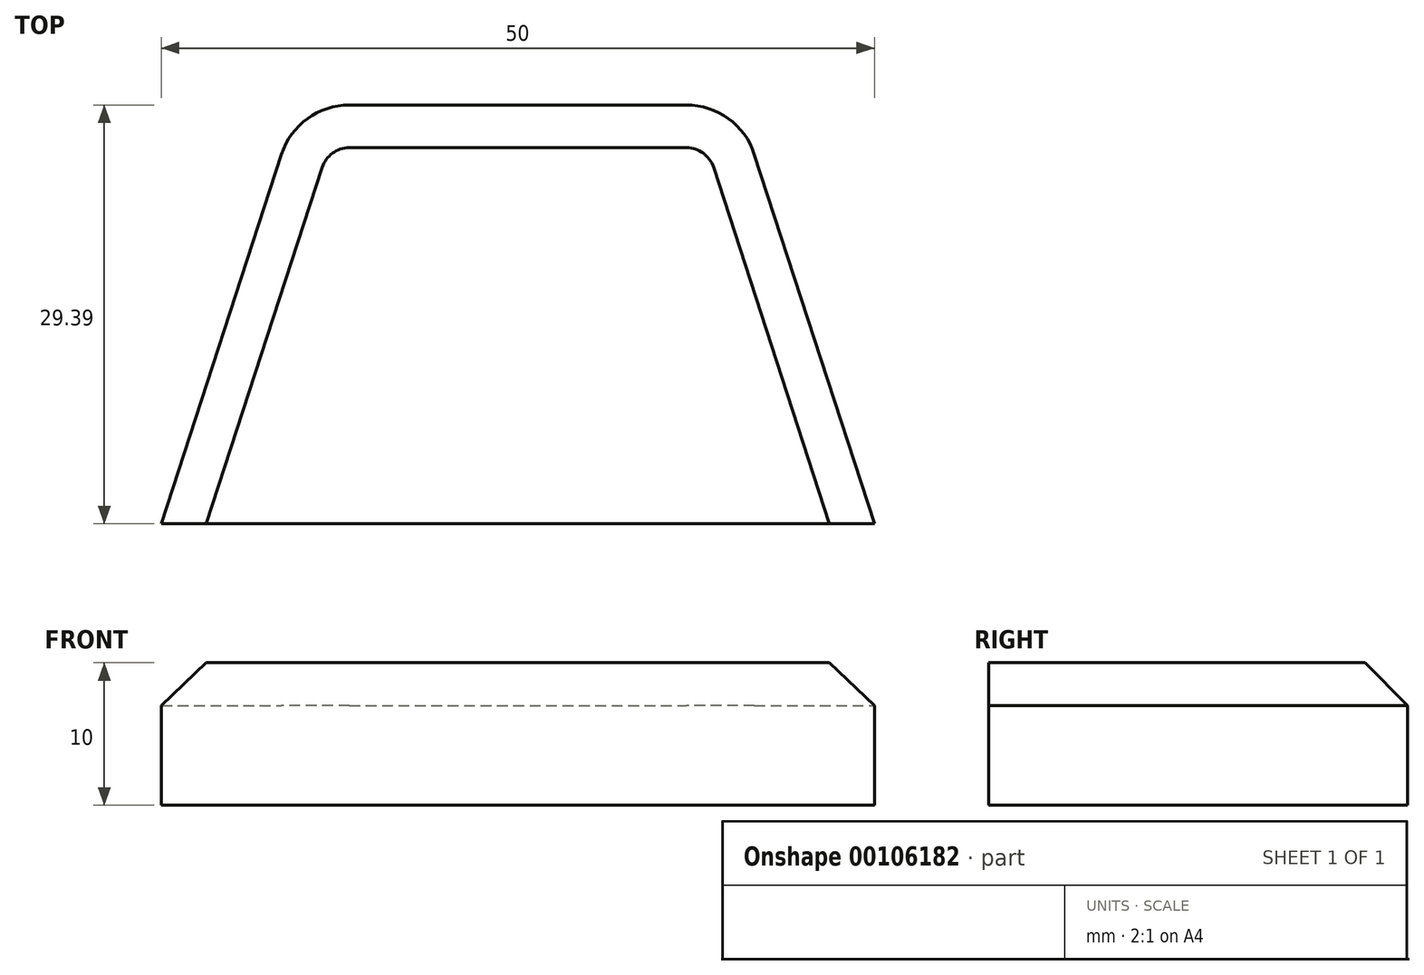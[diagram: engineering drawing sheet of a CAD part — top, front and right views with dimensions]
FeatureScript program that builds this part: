
annotation { "Feature Type Name" : "Feature", "Feature Type Description" : "" }
export const myFeature = defineFeature(function(context is Context, id is Id, definition is map)
    precondition{}
    {
        {
            var Q0;
            Q0=qCreatedBy(makeId("Top.planeOp"),FACE);
            var sketch = newSketch(context, id + "F0", { "sketchPlane" : qUnion([Q0])});
            skArc(sketch, "E0.cCircle", {"start": v(19.65, -8.12) * mm, "mid": v(0, 21.27) * mm, "end": v(-19.65, -8.12) * mm, "construction": true});
            skLineSegment(sketch, "E0.0", {"start": v(15.45, 21.27) * mm, "end": v(25, -8.12) * mm});
            skLineSegment(sketch, "E0.3", {"start": v(-25, -8.12) * mm, "end": v(-15.45, 21.27) * mm});
            skLineSegment(sketch, "E0.4", {"start": v(-15.45, 21.27) * mm, "end": v(15.45, 21.27) * mm});
            skPoint(sketch, "E0.0.midPoint", {"position": v(20.23, 6.57) * mm});
            skLineSegment(sketch, "E1", {"start": v(-25, -8.12) * mm, "end": v(25, -8.12) * mm});
            skSolve(sketch);
        }
        {
            var Q0;
            Q0=makeQuery(id+"F0.imprint","IMPRINT",FACE,{"disambiguationData":[TD([[makeQuery(id+"F0.imprint","IMPRINT",EDGE,{"derivedFrom":sQuery(id+"F0.wireOp",EDGE,"E0.0")}),-1.0]])]});
            extrude(context, id + "F1", {"entities" : qUnion([Q0]), "depth" : 10 * mm});
        }
        {
            var Q0;
            Q0=makeQuery(id+"F1.opExtrude","SWEPT_EDGE",EDGE,{"disambiguationData":[OSD([sQuery(id+"F0.wireOp",EDGE,"E0.0"),sQuery(id+"F0.wireOp",EDGE,"E0.4")])]});
            var Q1;
            Q1=makeQuery(id+"F1.opExtrude","SWEPT_EDGE",EDGE,{"disambiguationData":[OSD([sQuery(id+"F0.wireOp",EDGE,"E0.3"),sQuery(id+"F0.wireOp",EDGE,"E0.4")])]});
            fillet(context, id + "F2", {"entities" : qUnion([Q0, Q1]), "radius" : 5 * mm, "tangentPropagation" : true, "allowEdgeOverflow" : false});
        }
        {
            var Q0;
            Q0=makeQuery(id+"F1.opExtrude","CAP_EDGE",EDGE,{"disambiguationData":[OSD([sQuery(id+"F0.wireOp",EDGE,"E0.0")])],"isStart":false});
            var Q1;
            {var subQ0=sQuery(id+"F0.wireOp",EDGE,"E0.4");var subQ1=sQuery(id+"F0.wireOp",EDGE,"E0.0");Q1=makeQuery(id+"F2.opFillet","BLEND_EDGE",EDGE,{"blendedFrom":[makeQuery(id+"F1.opExtrude","SWEPT_EDGE",EDGE,{"disambiguationData":[OSD([subQ1,subQ0])]}),makeQuery(id+"F1.opExtrude","CAP_FACE",FACE,{"disambiguationData":[OSD([subQ1,sQuery(id+"F0.wireOp",EDGE,"E0.3"),subQ0,sQuery(id+"F0.wireOp",EDGE,"E1")])],"isStart":false})],"blendedInto":[makeQuery(id+"F1.opExtrude","CAP_FACE",FACE,{"disambiguationData":[OSD([subQ1,sQuery(id+"F0.wireOp",EDGE,"E0.3"),subQ0,sQuery(id+"F0.wireOp",EDGE,"E1")])],"isStart":false})]});}
            var Q2;
            Q2=makeQuery(id+"F1.opExtrude","CAP_EDGE",EDGE,{"disambiguationData":[OSD([sQuery(id+"F0.wireOp",EDGE,"E0.4")])],"isStart":false});
            var Q3;
            Q3=makeQuery(id+"F1.opExtrude","CAP_EDGE",EDGE,{"disambiguationData":[OSD([sQuery(id+"F0.wireOp",EDGE,"E0.3")])],"isStart":false});
            var Q4;
            {var subQ0=sQuery(id+"F0.wireOp",EDGE,"E0.4");var subQ1=sQuery(id+"F0.wireOp",EDGE,"E0.3");Q4=makeQuery(id+"F2.opFillet","BLEND_EDGE",EDGE,{"blendedFrom":[makeQuery(id+"F1.opExtrude","SWEPT_EDGE",EDGE,{"disambiguationData":[OSD([subQ1,subQ0])]}),makeQuery(id+"F1.opExtrude","CAP_FACE",FACE,{"disambiguationData":[OSD([sQuery(id+"F0.wireOp",EDGE,"E0.0"),subQ1,subQ0,sQuery(id+"F0.wireOp",EDGE,"E1")])],"isStart":false})],"blendedInto":[makeQuery(id+"F1.opExtrude","CAP_FACE",FACE,{"disambiguationData":[OSD([sQuery(id+"F0.wireOp",EDGE,"E0.0"),subQ1,subQ0,sQuery(id+"F0.wireOp",EDGE,"E1")])],"isStart":false})]});}
            chamfer(context, id + "F3", {"entities" : qUnion([Q0, Q1, Q2, Q3, Q4]), "width" : 3 * mm, "tangentPropagation" : true});
        }
    });
